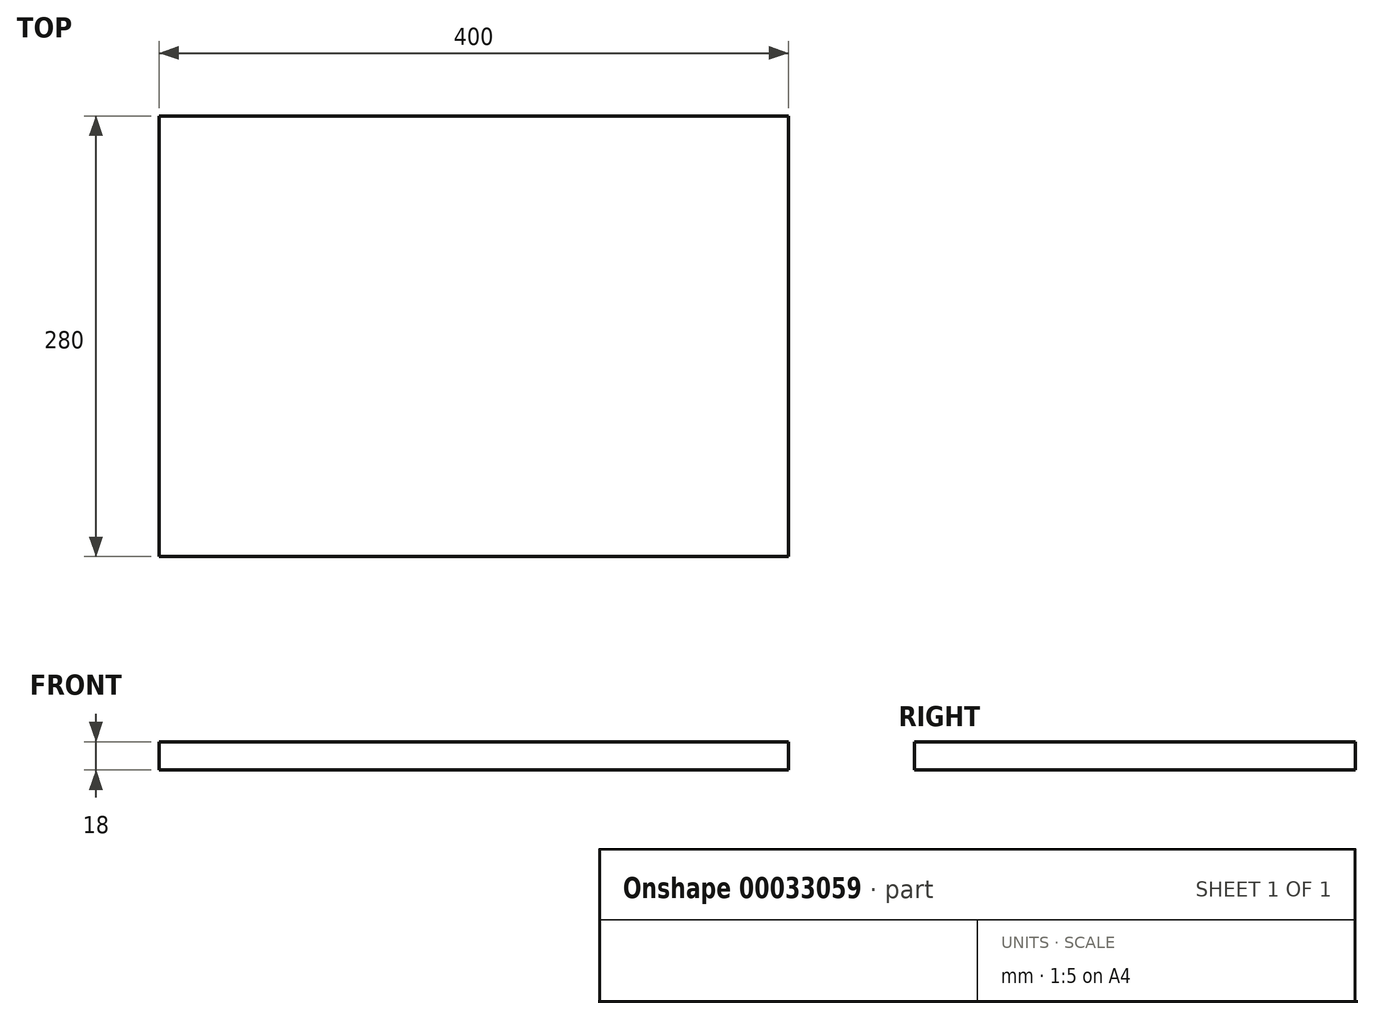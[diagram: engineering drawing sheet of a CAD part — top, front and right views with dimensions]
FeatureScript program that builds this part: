
annotation { "Feature Type Name" : "Feature", "Feature Type Description" : "" }
export const myFeature = defineFeature(function(context is Context, id is Id, definition is map)
    precondition{}
    {
        {
            var Q0;
            Q0=qCreatedBy(makeId("Top.planeOp"),FACE);
            var sketch = newSketch(context, id + "F0", { "sketchPlane" : qUnion([Q0])});
            skLineSegment(sketch, "E0.bottom", {"start": v(-200, 0) * mm, "end": v(200, 0) * mm});
            skLineSegment(sketch, "E0.top", {"start": v(-200, 280) * mm, "end": v(200, 280) * mm});
            skLineSegment(sketch, "E0.left", {"start": v(-200, 0) * mm, "end": v(-200, 280) * mm});
            skLineSegment(sketch, "E0.right", {"start": v(200, 0) * mm, "end": v(200, 280) * mm});
            skLineSegment(sketch, "E1", {"start": v(0, 185.28) * mm, "end": v(0, -60.67) * mm, "construction": true});
            skSolve(sketch);
        }
        {
            var Q0;
            Q0 = qSketchRegion(id + "F0", true);
            extrude(context, id + "F1", {"entities" : qUnion([Q0]), "depth" : 18 * mm});
        }
    });
